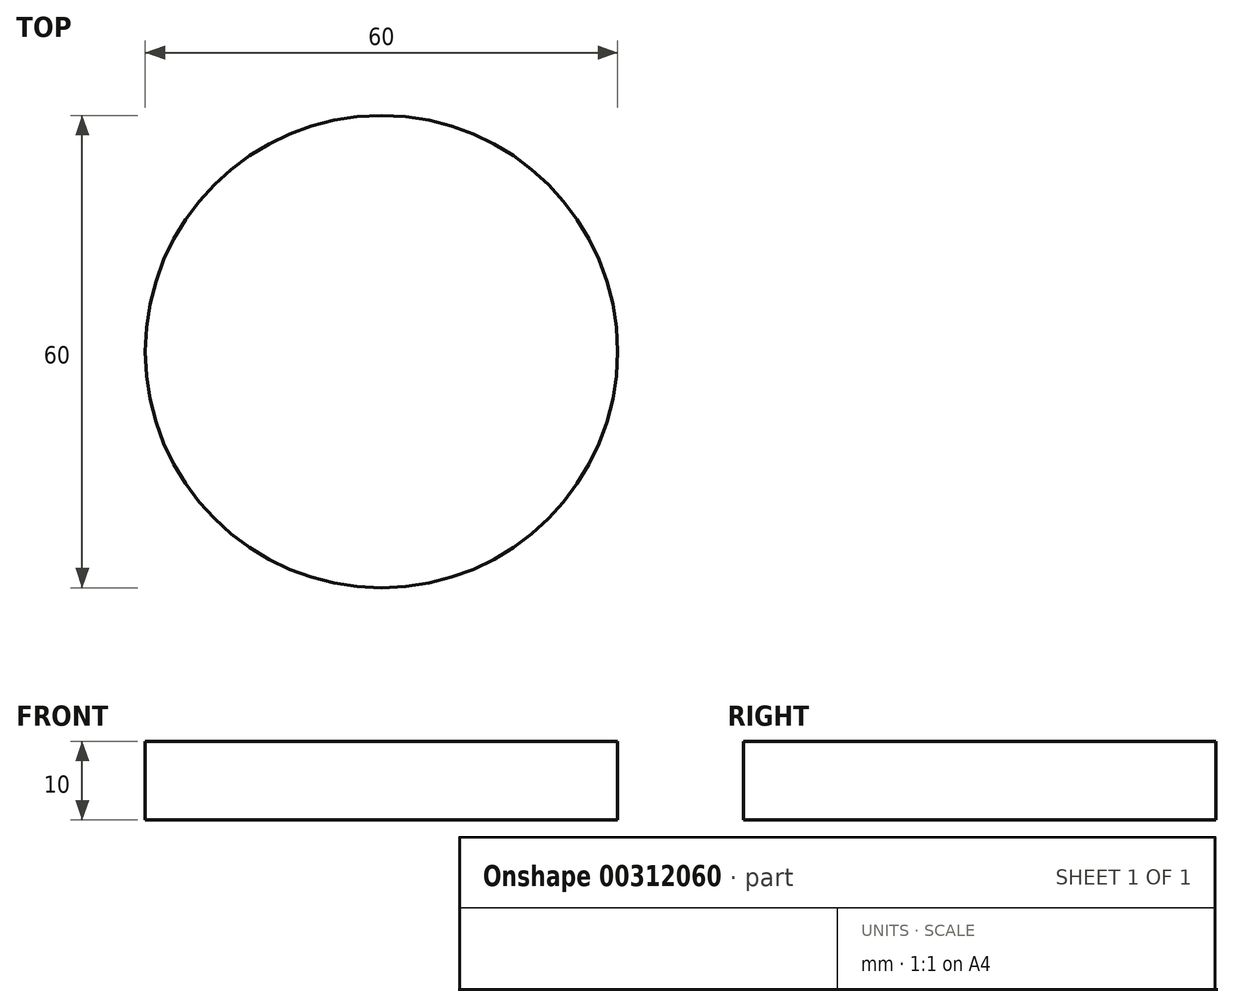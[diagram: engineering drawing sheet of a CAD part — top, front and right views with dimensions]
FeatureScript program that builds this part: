
annotation { "Feature Type Name" : "Feature", "Feature Type Description" : "" }
export const myFeature = defineFeature(function(context is Context, id is Id, definition is map)
    precondition{}
    {
        {
            var Q0;
            Q0=qCreatedBy(makeId("Top.planeOp"),FACE);
            var sketch = newSketch(context, id + "F0", { "sketchPlane" : qUnion([Q0])});
            skCircle(sketch, "E0", {"center": v(0, 0) * mm, "radius": 30 * mm});
            skSolve(sketch);
        }
        {
            var Q0;
            Q0 = qSketchRegion(id + "F0", true);
            extrude(context, id + "F1", {"entities" : qUnion([Q0]), "depth" : 10 * mm});
        }
    });
